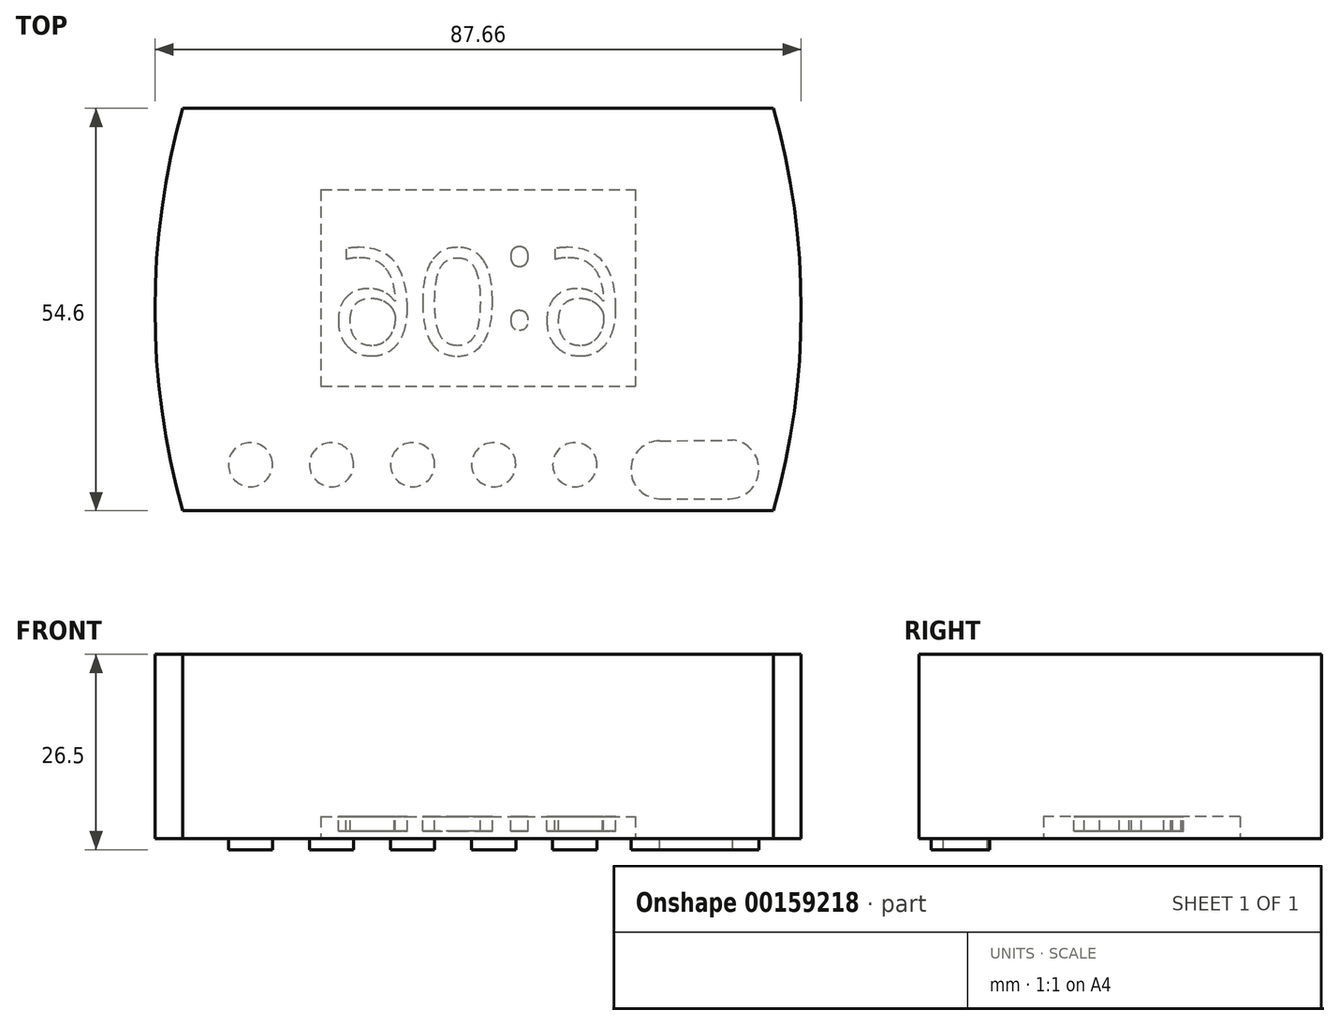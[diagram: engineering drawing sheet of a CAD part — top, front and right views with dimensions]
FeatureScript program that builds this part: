
annotation { "Feature Type Name" : "Feature", "Feature Type Description" : "" }
export const myFeature = defineFeature(function(context is Context, id is Id, definition is map)
    precondition{}
    {
        {
            var Q0;
            Q0=qCreatedBy(makeId("Top.planeOp"),FACE);
            var sketch = newSketch(context, id + "F0", { "sketchPlane" : qUnion([Q0])});
            skLineSegment(sketch, "E0.bottom", {"start": v(-40.08, 27.3) * mm, "end": v(40.08, 27.3) * mm});
            skLineSegment(sketch, "E0.top", {"start": v(-40.08, -27.3) * mm, "end": v(40.08, -27.3) * mm});
            skPoint(sketch, "E0.middle", {"position": v(0, 0) * mm});
            skArc(sketch, "E1", {"start": v(40.07, -27.3) * mm, "mid": v(43.83, 0) * mm, "end": v(40.08, 27.3) * mm});
            skArc(sketch, "E2.MirrorCS", {"start": v(-40.07, -27.3) * mm, "mid": v(-43.83, 0) * mm, "end": v(-40.08, 27.3) * mm});
            skSolve(sketch);
        }
        {
            var Q0;
            Q0 = qSketchRegion(id + "F0", true);
            extrude(context, id + "F1", {"entities" : qUnion([Q0]), "depth" : 25 * mm});
        }
        {
            var Q0;
            Q0=qCreatedBy(makeId("Top.planeOp"),FACE);
            var sketch = newSketch(context, id + "F2", { "sketchPlane" : qUnion([Q0])});
            skLineSegment(sketch, "E3.bottom", {"start": v(-21.33, 16.27) * mm, "end": v(21.33, 16.27) * mm});
            skLineSegment(sketch, "E3.top", {"start": v(-21.33, -10.4) * mm, "end": v(21.33, -10.4) * mm});
            skLineSegment(sketch, "E3.left", {"start": v(-21.33, 16.27) * mm, "end": v(-21.33, -10.4) * mm});
            skLineSegment(sketch, "E3.right", {"start": v(21.33, 16.27) * mm, "end": v(21.33, -10.4) * mm});
            skSolve(sketch);
        }
        {
            var Q0;
            Q0 = qSketchRegion(id + "F2", true);
            extrude(context, id + "F3", {"entities" : qUnion([Q0]), "operationType" : NewBodyOperationType.REMOVE, "depth" : 3 * mm});
        }
        {
            var Q0;
            Q0=qCreatedBy(makeId("Top.planeOp"),FACE);
            var sketch = newSketch(context, id + "F4", { "sketchPlane" : qUnion([Q0])});
            skCircle(sketch, "E4", {"center": v(-30.88, -21.05) * mm, "radius": 3 * mm});
            skCircle(sketch, "E5.1.0.0", {"center": v(-19.88, -21.05) * mm, "radius": 3 * mm});
            skCircle(sketch, "E5.2.0.0", {"center": v(-8.88, -21.05) * mm, "radius": 3 * mm});
            skCircle(sketch, "E5.3.0.0", {"center": v(2.12, -21.05) * mm, "radius": 3 * mm});
            skCircle(sketch, "E5.4.0.0", {"center": v(13.12, -21.05) * mm, "radius": 3 * mm});
            skLineSegment(sketch, "E5.direction1", {"start": v(-30.88, -21.05) * mm, "end": v(-19.88, -21.05) * mm, "construction": true});
            skLineSegment(sketch, "E6.bottom", {"start": v(13.26, -43.3) * mm, "end": v(24.73, -43.3) * mm});
            skPoint(sketch, "E7", {"position": v(-3.25, -26.78) * mm});
            skPoint(sketch, "E8", {"position": v(5.94, -26.78) * mm});
            skLineSegment(sketch, "E9", {"start": v(24.66, -25.67) * mm, "end": v(34.12, -25.67) * mm});
            skLineSegment(sketch, "E10.MirrorCS", {"start": v(24.66, -17.82) * mm, "end": v(34.55, -17.72) * mm});
            skPoint(sketch, "E11.start.orphan", {"position": v(-1969.82, 0) * mm});
            skArc(sketch, "E12", {"start": v(24.66, -25.67) * mm, "mid": v(20.73, -21.75) * mm, "end": v(24.66, -17.82) * mm});
            skArc(sketch, "E13", {"start": v(34.12, -25.67) * mm, "mid": v(38.1, -21.9) * mm, "end": v(34.55, -17.72) * mm});
            skPoint(sketch, "E14.visualSharp", {"position": v(24.66, -25.67) * mm});
            skLineSegment(sketch, "E14.filletArc", {"start": v(24.66, -25.67) * mm, "end": v(24.66, -25.67) * mm});
            skSolve(sketch);
        }
        {
            var Q0;
            Q0 = qSketchRegion(id + "F4", true);
            extrude(context, id + "F5", {"entities" : qUnion([Q0]), "operationType" : NewBodyOperationType.ADD, "oppositeDirection" : true, "depth" : 1.5 * mm});
        }
        {
            var Q0;
            Q0=makeQuery(id+"F3.boolean.opBoolean","COPY",FACE,{"derivedFrom":makeQuery(id+"F3.opExtrude","CAP_FACE",FACE,{"disambiguationData":[OSD([sQuery(id+"F2.wireOp",EDGE,"E3.bottom"),sQuery(id+"F2.wireOp",EDGE,"E3.top"),sQuery(id+"F2.wireOp",EDGE,"E3.left"),sQuery(id+"F2.wireOp",EDGE,"E3.right")])],"isStart":false})});
            var sketch = newSketch(context, id + "F6", { "sketchPlane" : qUnion([Q0])});
            skText(sketch, "E15", { "text": "90:9\n", "fontName": "OpenSans-Regular.ttf"});
            const initialGuessF6  = {"E15": [-0.02, -0.00824, 1, 0, 0.01445]};
            skSetInitialGuess(sketch, initialGuessF6);
            skSolve(sketch);
        }
        {
            var Q0;
            Q0 = qSketchRegion(id + "F6", true);
            extrude(context, id + "F7", {"entities" : qUnion([Q0]), "operationType" : NewBodyOperationType.ADD, "depth" : 2 * mm});
        }
    });
